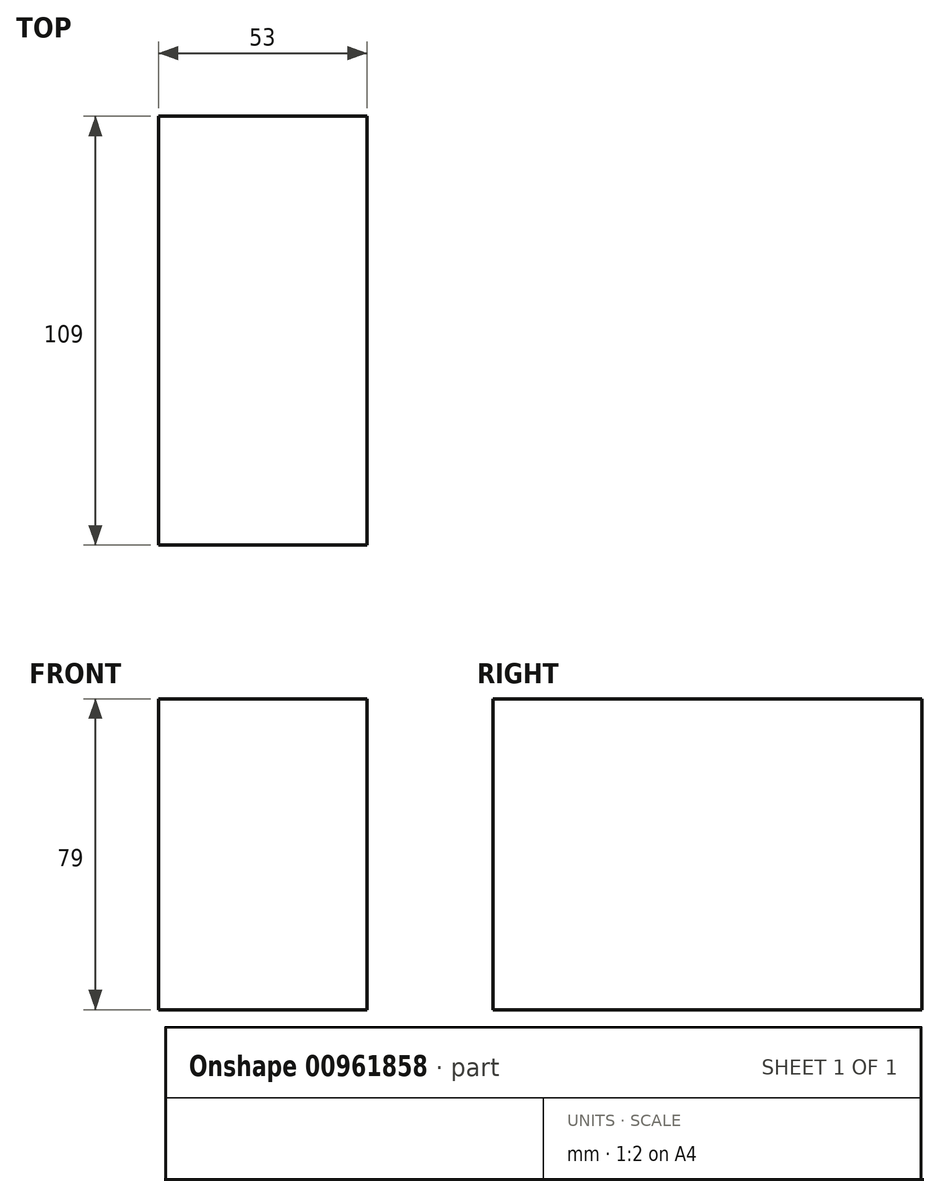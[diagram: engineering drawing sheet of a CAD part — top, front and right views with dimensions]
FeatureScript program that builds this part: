
annotation { "Feature Type Name" : "Feature", "Feature Type Description" : "" }
export const myFeature = defineFeature(function(context is Context, id is Id, definition is map)
    precondition{}
    {
        {
            var Q0;
            Q0=qCreatedBy(makeId("Top.planeOp"),FACE);
            var sketch = newSketch(context, id + "F0", { "sketchPlane" : qUnion([Q0])});
            skLineSegment(sketch, "E0.bottom", {"start": v(-68.61, 75.2) * mm, "end": v(-15.61, 75.2) * mm});
            skLineSegment(sketch, "E0.top", {"start": v(-68.61, -33.8) * mm, "end": v(-15.61, -33.8) * mm});
            skLineSegment(sketch, "E0.left", {"start": v(-68.61, 75.2) * mm, "end": v(-68.61, -33.8) * mm});
            skLineSegment(sketch, "E0.right", {"start": v(-15.61, 75.2) * mm, "end": v(-15.61, -33.8) * mm});
            skSolve(sketch);
        }
        {
            var Q0;
            Q0 = qSketchRegion(id + "F0", true);
            extrude(context, id + "F1", {"entities" : qUnion([Q0]), "depth" : 79 * mm, "offsetDistance" : 25 * mm});
        }
    });
